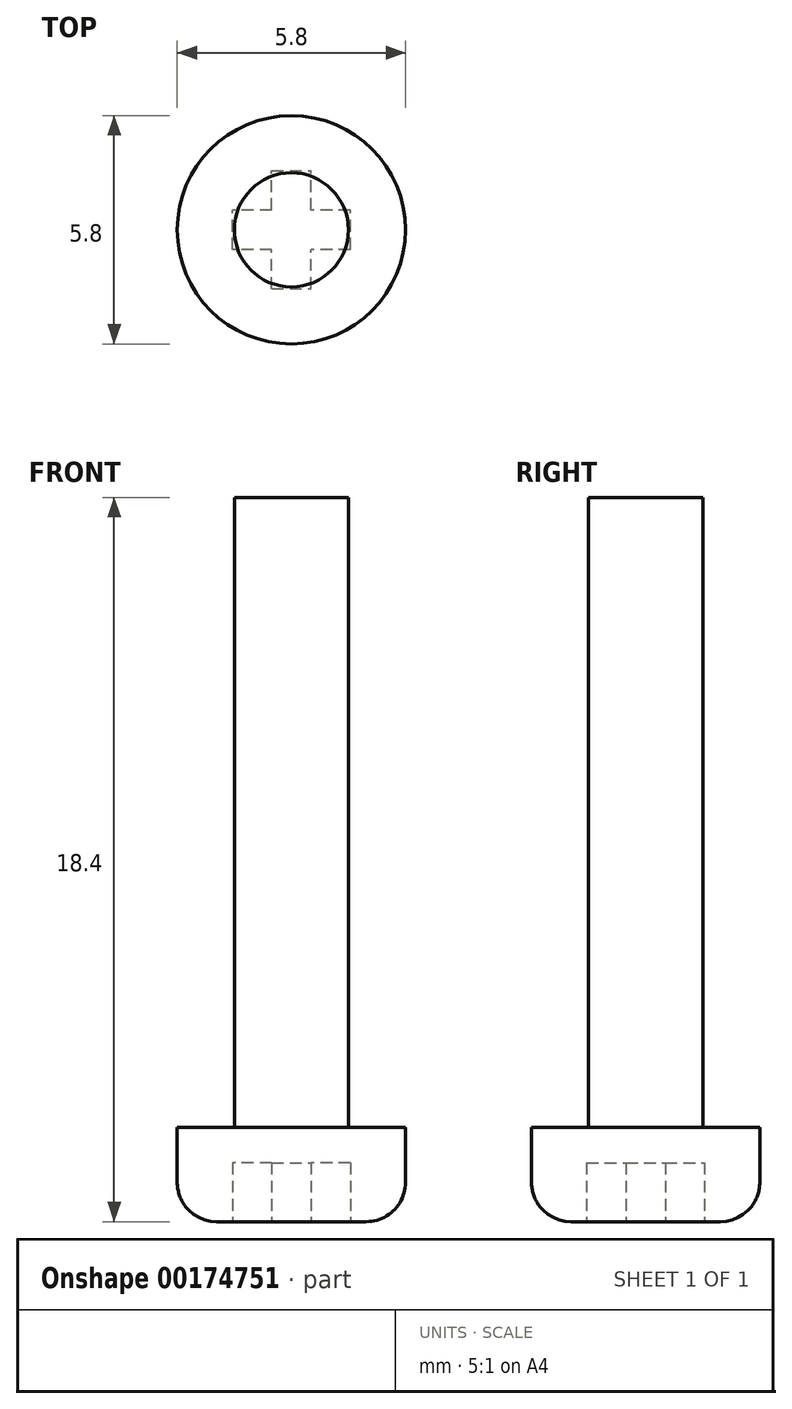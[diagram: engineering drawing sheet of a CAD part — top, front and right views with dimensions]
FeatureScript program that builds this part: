
annotation { "Feature Type Name" : "Feature", "Feature Type Description" : "" }
export const myFeature = defineFeature(function(context is Context, id is Id, definition is map)
    precondition{}
    {
        {
            var Q0;
            Q0=qCreatedBy(makeId("Top.planeOp"),FACE);
            var sketch = newSketch(context, id + "F0", { "sketchPlane" : qUnion([Q0])});
            skCircle(sketch, "E0", {"center": v(0, 0) * mm, "radius": 1.45 * mm});
            skSolve(sketch);
        }
        {
            var Q0;
            Q0 = qSketchRegion(id + "F0", true);
            extrude(context, id + "F1", {"entities" : qUnion([Q0]), "depth" : 16 * mm});
        }
        {
            var Q0;
            Q0=qCreatedBy(makeId("Top.planeOp"),FACE);
            var sketch = newSketch(context, id + "F2", { "sketchPlane" : qUnion([Q0])});
            skCircle(sketch, "E1", {"center": v(0, 0) * mm, "radius": 2.9 * mm});
            skSolve(sketch);
        }
        {
            var Q0;
            Q0 = qSketchRegion(id + "F2", true);
            extrude(context, id + "F3", {"entities" : qUnion([Q0]), "operationType" : NewBodyOperationType.ADD, "oppositeDirection" : true, "depth" : 2.4 * mm});
        }
        {
            var Q0;
            Q0=makeQuery(id+"F3.opExtrude","CAP_EDGE",EDGE,{"disambiguationData":[OSD([sQuery(id+"F2.wireOp",EDGE,"E1")])],"isStart":false});
            fillet(context, id + "F4", {"entities" : qUnion([Q0]), "radius" : 1 * mm, "tangentPropagation" : true, "allowEdgeOverflow" : false});
        }
        {
            var Q0;
            Q0=makeQuery(id+"F3.opExtrude","CAP_FACE",FACE,{"disambiguationData":[OSD([sQuery(id+"F2.wireOp",EDGE,"E1")])],"isStart":false});
            var sketch = newSketch(context, id + "F5", { "sketchPlane" : qUnion([Q0])});
            skLineSegment(sketch, "E2.bottom", {"start": v(1.5, 0.5) * mm, "end": v(-1.5, 0.5) * mm});
            skLineSegment(sketch, "E2.top", {"start": v(1.5, -0.5) * mm, "end": v(-1.5, -0.5) * mm});
            skLineSegment(sketch, "E2.left", {"start": v(1.5, 0.5) * mm, "end": v(1.5, -0.5) * mm});
            skLineSegment(sketch, "E2.right", {"start": v(-1.5, 0.5) * mm, "end": v(-1.5, -0.5) * mm});
            skPoint(sketch, "E2.middle", {"position": v(0, 0) * mm});
            skLineSegment(sketch, "E3.bottom", {"start": v(-0.5, 1.5) * mm, "end": v(0.5, 1.5) * mm});
            skLineSegment(sketch, "E3.top", {"start": v(-0.5, -1.5) * mm, "end": v(0.5, -1.5) * mm});
            skLineSegment(sketch, "E3.left", {"start": v(-0.5, 1.5) * mm, "end": v(-0.5, -1.5) * mm});
            skLineSegment(sketch, "E3.right", {"start": v(0.5, 1.5) * mm, "end": v(0.5, -1.5) * mm});
            skSolve(sketch);
        }
        {
            var Q0;
            Q0 = qSketchRegion(id + "F5", true);
            extrude(context, id + "F6", {"entities" : qUnion([Q0]), "operationType" : NewBodyOperationType.REMOVE, "oppositeDirection" : true, "depth" : 1.5 * mm});
        }
    });
